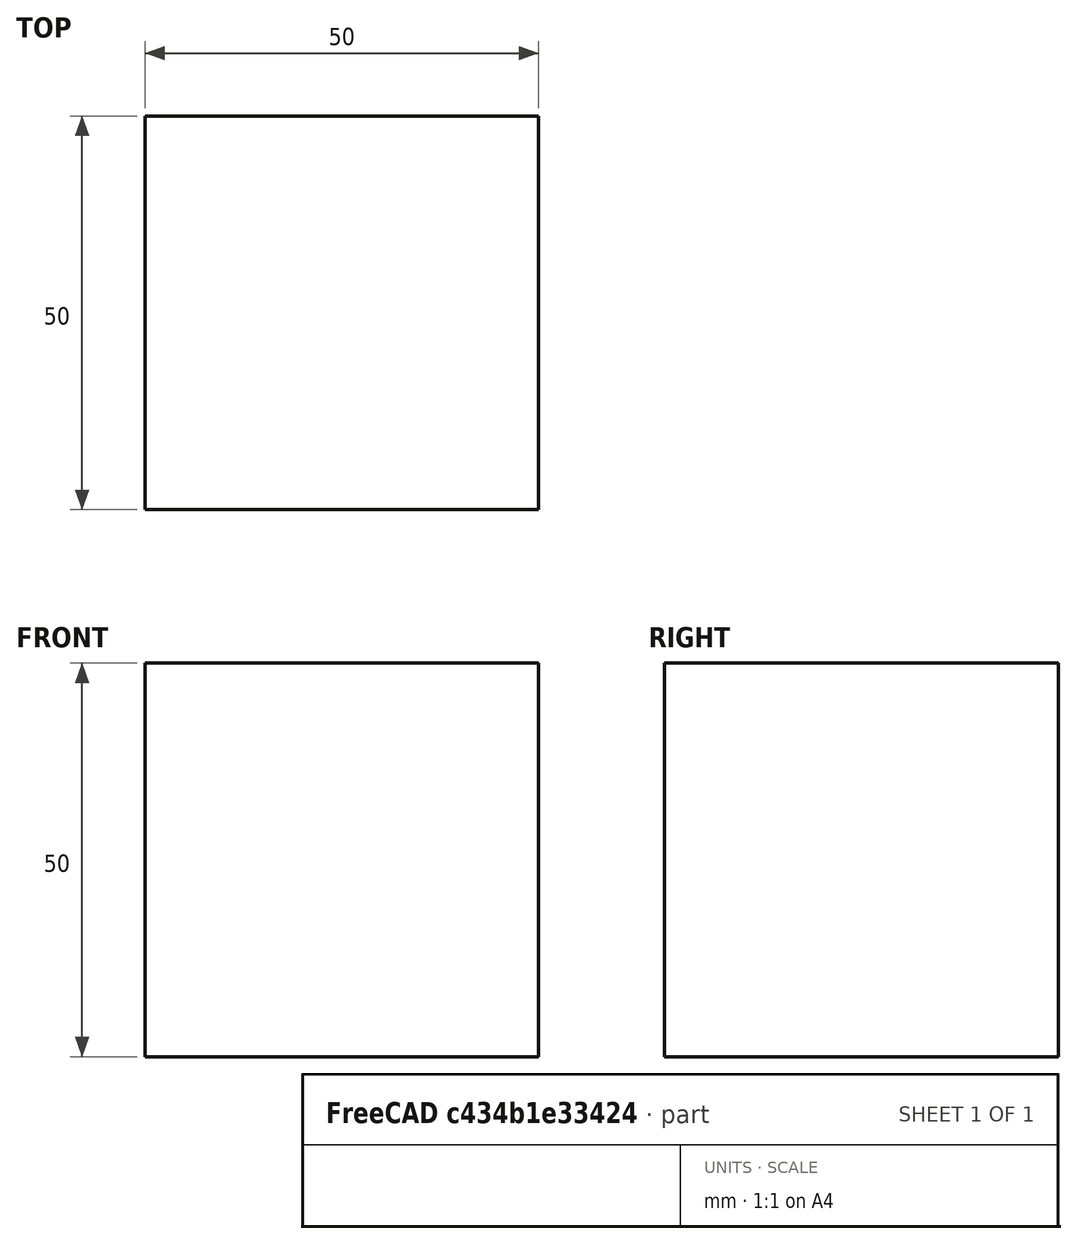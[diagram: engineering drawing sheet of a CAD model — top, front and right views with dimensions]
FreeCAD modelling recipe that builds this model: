
FCSTD DOCUMENT  (FreeCAD 0.15R4671 (Git))
Label: Square Bar 50 EN10059 S235JR
License: All rights reserved
LicenseURL: http://en.wikipedia.org/wiki/All_rights_reserved
objects: Sketcher::SketchObject×1, Part::Extrusion×1
note: 2 computed .brp shape members not serialized (recipe doc carries the construction recipe); baked Part::Feature solids carry a one-line shape summary decoded from their .brp

FEATURE [Sketcher::SketchObject] Sketch
  sketch-geometry (4):
    g0: LineSegment StartX=-25 StartY=-25 StartZ=0 EndX=25 EndY=-25 EndZ=0
    g1: LineSegment StartX=25 StartY=-25 StartZ=0 EndX=25 EndY=25 EndZ=0
    g2: LineSegment StartX=25 StartY=25 StartZ=0 EndX=-25 EndY=25 EndZ=0
    g3: LineSegment StartX=-25 StartY=25 StartZ=0 EndX=-25 EndY=-25 EndZ=0
  constraints (12):
    c: Coincident(g0,g1)
    c: Coincident(g1,g2)
    c: Coincident(g2,g3)
    c: Coincident(g3,g0)
    c: Horizontal(g0)
    c: Horizontal(g2)
    c: Vertical(g1)
    c: Vertical(g3)
    c: Symmetric(g1,g0,g-1)
    c: Symmetric(g2,g1,g-2)
    c: Equal(g1,g2)
    c: DistanceY(g1) = 50
FEATURE [Part::Extrusion] Extrude  label="Square Bar 50 EN10059 S235JR"
  Base = -> Sketch
  Dir = (0,0,50)
  Solid = true
